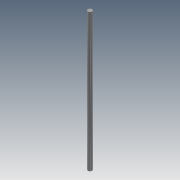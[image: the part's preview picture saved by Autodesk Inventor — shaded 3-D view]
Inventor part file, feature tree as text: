
AUTODESK INVENTOR PART (.ipt)
format: ipt  version: 2013 (Build 170138000, 138)  size: 71,168 bytes
history: native  units: mm
features: sketch x3, extrude x1
ambient origin geometry x8: Origin, YZ Plane, XZ Plane, XY Plane, X Axis, Y Axis, Z Axis, Center Point
bodies: Solid1 (feature_tree)
feature tree (4):
  sketch  "Sketch1"  dims[d1=6.0mm d2=200.0mm d3=0.0mm]
  sketch  "Sketch2"
  extrude  "Extrusion1"  Depth=200.0mm TaperAngle=0.0deg
  sketch  "Sketch3"
